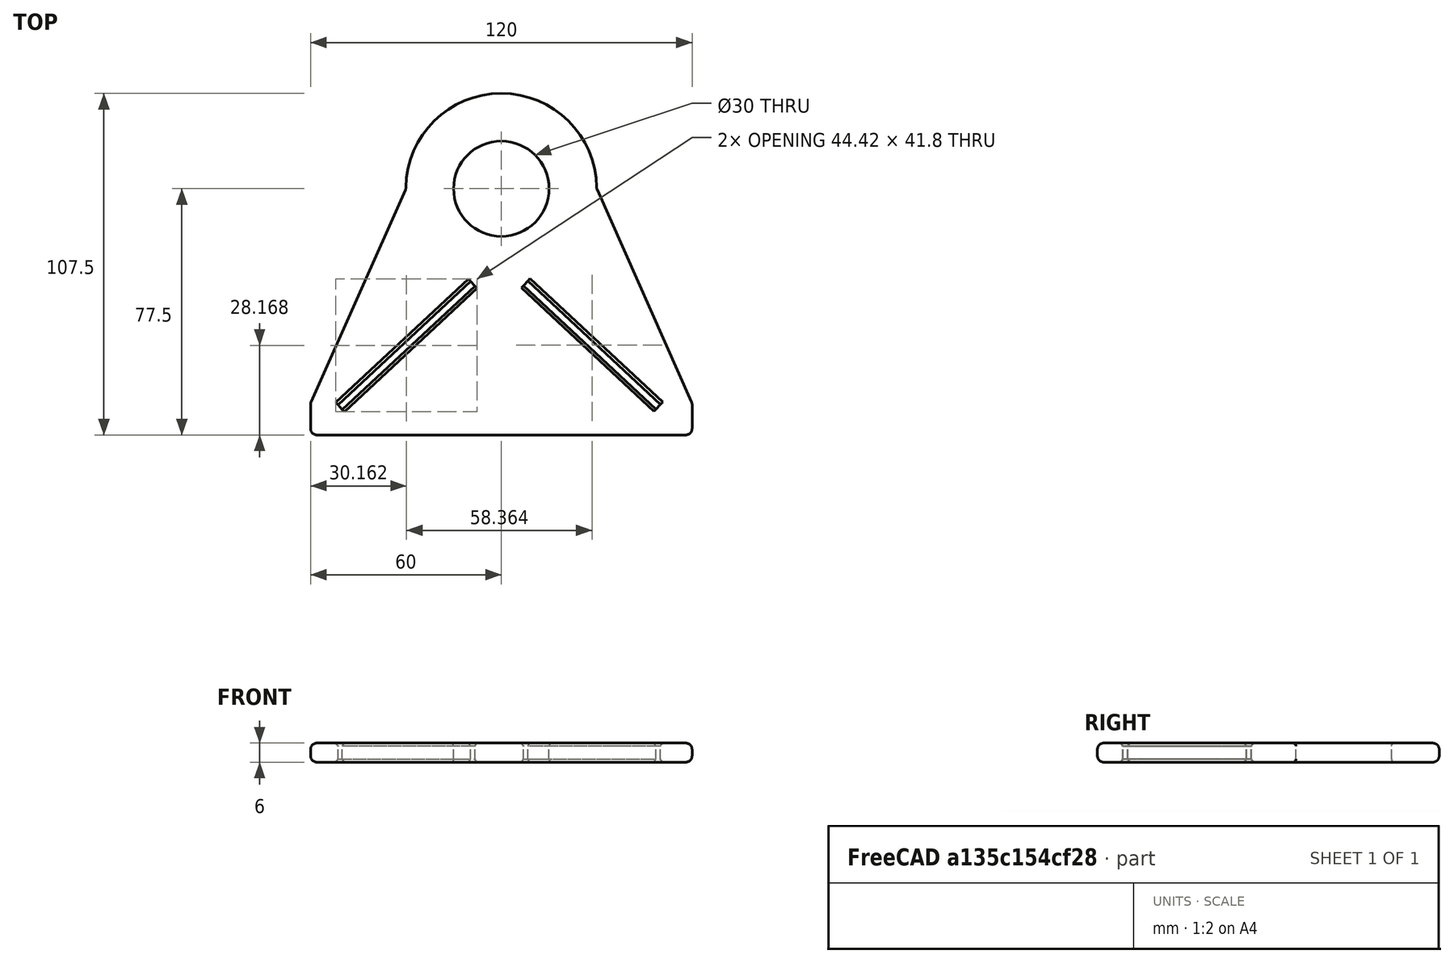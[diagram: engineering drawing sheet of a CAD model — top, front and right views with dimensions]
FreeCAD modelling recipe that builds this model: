
FCSTD DOCUMENT  (FreeCAD 0.18R4 (GitTag))
Label: EndPin
License: All rights reserved
LicenseURL: http://en.wikipedia.org/wiki/All_rights_reserved
objects: Part::Box×3, Part::Cylinder×2, Part::MultiFuse×2, Part::Fillet×2, Part::Wedge×1, Part::Cut×1, Part::Chamfer×1
note: 12 computed .brp shape members not serialized (recipe doc carries the construction recipe); baked Part::Feature solids carry a one-line shape summary decoded from their .brp

FEATURE [Part::Cylinder] Cylinder
  Angle = 360
  AttacherType = Attacher::AttachEngine3D
  Height = 10
  Placement = pos=(0,7.5,0) rot=(0,0,1;0rad)
  Radius = 15
FEATURE [Part::Cylinder] Cylinder001
  Angle = 360
  AttacherType = Attacher::AttachEngine3D
  Height = 6
  Placement = pos=(0,7.5,0) rot=(0,0,1;0rad)
  Radius = 30
FEATURE [Part::Box] Box002  label="Buckle001"
  AttacherType = Attacher::AttachEngine3D
  Height = 10
  Length = 57
  Placement = pos=(7,-23,0) rot=(0,0,-1;0.750492rad)
  Width = 2
FEATURE [Part::Box] Box003  label="Buckle002"
  AttacherType = Attacher::AttachEngine3D
  Height = 10
  Length = 57
  Placement = pos=(-50,-62,0) rot=(0,0,1;0.750492rad)
  Width = 2
FEATURE [Part::Box] Box  label="Cube"
  AttacherType = Attacher::AttachEngine3D
  Height = 6
  Length = 120
  Placement = pos=(-60,-70,0) rot=(0,0,1;0rad)
  Width = 10
FEATURE [Part::Wedge] Wedge
  AttacherType = Attacher::AttachEngine3D
  Placement = pos=(0,-50,0) rot=(0,0,1;0rad)
  X2max = 30
  X2min = -30
  Xmax = 60
  Xmin = -60
  Ymax = 57.5
  Ymin = -10
  Z2max = 6
  Z2min = 0
  Zmax = 6
  Zmin = 0
FEATURE [Part::MultiFuse] Fusion001  label="holders"
  Refine = true
  Shapes = -> [Box003,Box002,Cylinder]
FEATURE [Part::MultiFuse] Fusion  label="Base"
  Refine = true
  Shapes = -> [Cylinder001,Wedge,Box]
FEATURE [Part::Fillet] Fillet
  Base = -> Fusion
  Edges = 18 edges r=2: [Edge1,Edge2,Edge3,Edge4,Edge5,Edge6,Edge7,Edge8,Edge9,Edge10,Edge11,Edge12,Edge13,Edge14,Edge15,Edge16,Edge17,Edge18]
FEATURE [Part::Cut] Cut
  Base = -> Fillet
  Refine = true
  Tool = -> Fusion001
FEATURE [Part::Fillet] Fillet001
  Base = -> Cut
  Edges = 2 edges r=1: [Edge31,Edge48]
FEATURE [Part::Chamfer] Chamfer
  Base = -> Fillet001
  Edges = 8 edges r=1: [Edge10,Edge12,Edge14,Edge16,Edge41,Edge45,Edge49,Edge53]
